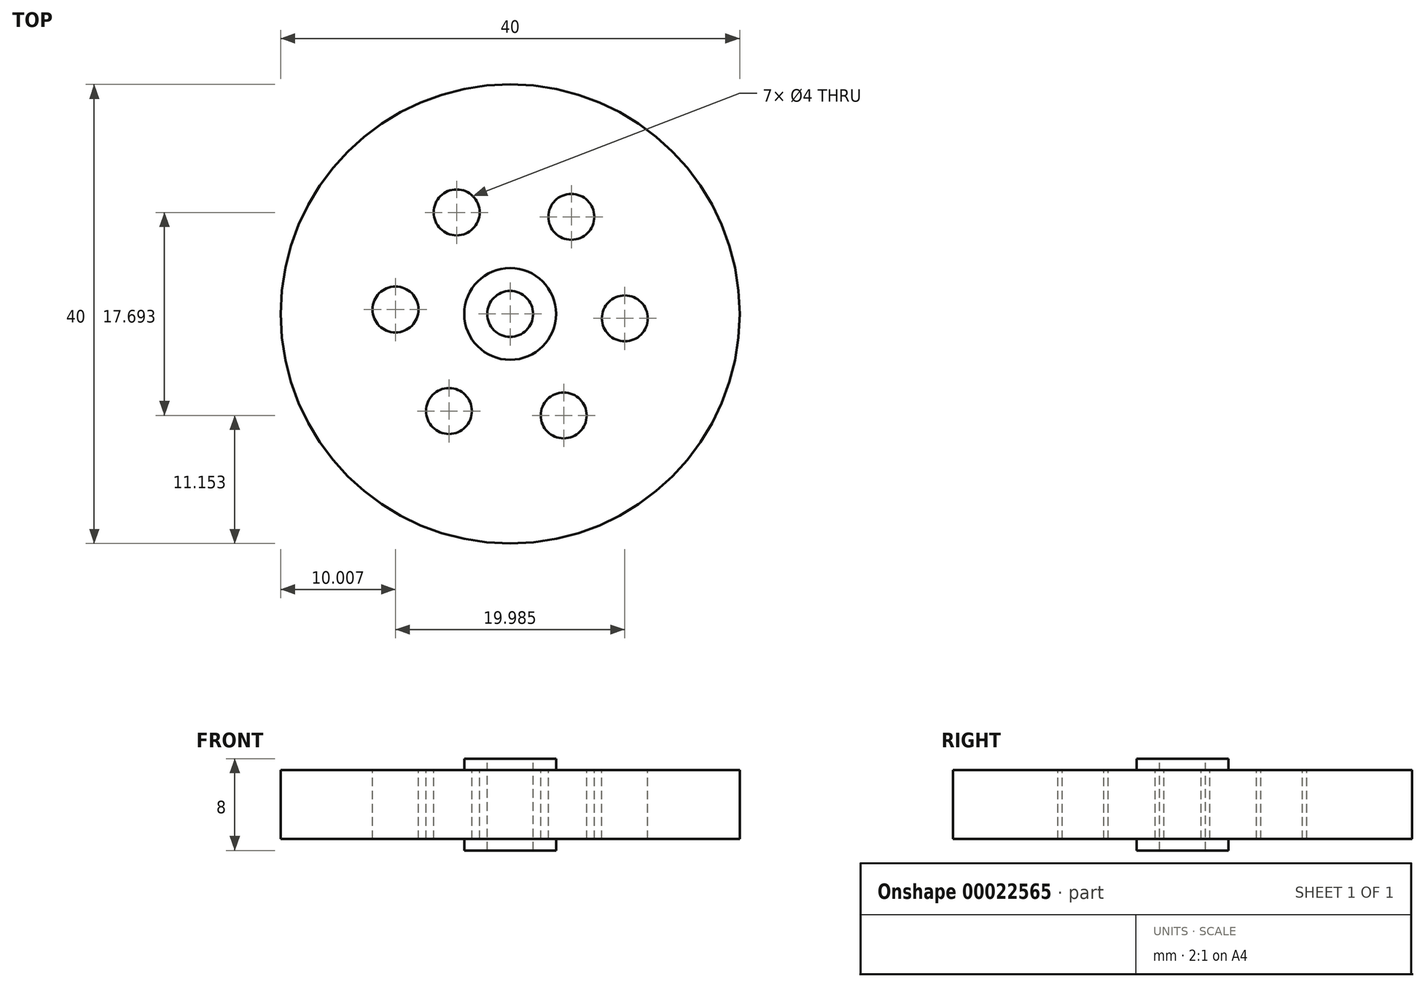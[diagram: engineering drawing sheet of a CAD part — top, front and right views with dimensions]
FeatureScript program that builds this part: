
annotation { "Feature Type Name" : "Feature", "Feature Type Description" : "" }
export const myFeature = defineFeature(function(context is Context, id is Id, definition is map)
    precondition{}
    {
        {
            var Q0;
            Q0=qCreatedBy(makeId("Top.planeOp"),FACE);
            var sketch = newSketch(context, id + "F0", { "sketchPlane" : qUnion([Q0])});
            skCircle(sketch, "E0", {"center": v(0, 0) * mm, "radius": 20 * mm});
            skSolve(sketch);
        }
        {
            var Q0;
            Q0=makeQuery(id+"F0.imprint","IMPRINT",FACE,{"disambiguationData":[TD([[makeQuery(id+"F0.imprint","IMPRINT",EDGE,{"derivedFrom":sQuery(id+"F0.wireOp",EDGE,"E0")}),1.0]])]});
            extrude(context, id + "F1", {"entities" : qUnion([Q0]), "depth" : 6 * mm});
        }
        {
            var Q0;
            Q0=makeQuery(id+"F1.opExtrude","CAP_FACE",FACE,{"disambiguationData":[OSD([sQuery(id+"F0.wireOp",EDGE,"E0")])],"isStart":false});
            var sketch = newSketch(context, id + "F2", { "sketchPlane" : qUnion([Q0])});
            skCircle(sketch, "E1", {"center": v(0, 0) * mm, "radius": 4 * mm});
            skCircle(sketch, "E2", {"center": v(0, 0) * mm, "radius": 2 * mm});
            skCircle(sketch, "E3", {"center": v(5.33, 8.46) * mm, "radius": 2 * mm});
            skCircle(sketch, "E4.1.0", {"center": v(-4.66, 8.85) * mm, "radius": 2 * mm});
            skCircle(sketch, "E4.2.0", {"center": v(-10, 0.39) * mm, "radius": 2 * mm});
            skCircle(sketch, "E4.3.0", {"center": v(-5.33, -8.46) * mm, "radius": 2 * mm});
            skCircle(sketch, "E4.4.0", {"center": v(4.66, -8.85) * mm, "radius": 2 * mm});
            skCircle(sketch, "E4.5.0", {"center": v(10, -0.39) * mm, "radius": 2 * mm});
            skSolve(sketch);
        }
        {
            var Q0;
            Q0=makeQuery(id+"F2.imprint","IMPRINT",FACE,{"disambiguationData":[TD([[makeQuery(id+"F2.imprint","IMPRINT",EDGE,{"derivedFrom":sQuery(id+"F2.wireOp",EDGE,"E4.1.0")}),1.0]])]});
            var Q1;
            Q1=makeQuery(id+"F2.imprint","IMPRINT",FACE,{"disambiguationData":[TD([[makeQuery(id+"F2.imprint","IMPRINT",EDGE,{"derivedFrom":sQuery(id+"F2.wireOp",EDGE,"E3")}),1.0]])]});
            var Q2;
            Q2=makeQuery(id+"F2.imprint","IMPRINT",FACE,{"disambiguationData":[TD([[makeQuery(id+"F2.imprint","IMPRINT",EDGE,{"derivedFrom":sQuery(id+"F2.wireOp",EDGE,"E4.5.0")}),1.0]])]});
            var Q3;
            Q3=makeQuery(id+"F2.imprint","IMPRINT",FACE,{"disambiguationData":[TD([[makeQuery(id+"F2.imprint","IMPRINT",EDGE,{"derivedFrom":sQuery(id+"F2.wireOp",EDGE,"E4.4.0")}),1.0]])]});
            var Q4;
            Q4=makeQuery(id+"F2.imprint","IMPRINT",FACE,{"disambiguationData":[TD([[makeQuery(id+"F2.imprint","IMPRINT",EDGE,{"derivedFrom":sQuery(id+"F2.wireOp",EDGE,"E4.3.0")}),1.0]])]});
            var Q5;
            Q5=makeQuery(id+"F2.imprint","IMPRINT",FACE,{"disambiguationData":[TD([[makeQuery(id+"F2.imprint","IMPRINT",EDGE,{"derivedFrom":sQuery(id+"F2.wireOp",EDGE,"E4.2.0")}),1.0]])]});
            var Q6;
            Q6=makeQuery(id+"F2.imprint","IMPRINT",FACE,{"disambiguationData":[TD([[makeQuery(id+"F2.imprint","IMPRINT",EDGE,{"derivedFrom":sQuery(id+"F2.wireOp",EDGE,"E2")}),1.0]])]});
            extrude(context, id + "F3", {"entities" : qUnion([Q0, Q1, Q2, Q3, Q4, Q5, Q6]), "operationType" : NewBodyOperationType.REMOVE, "endBound" : BoundingType.THROUGH_ALL, "oppositeDirection" : true, "depth" : 25.4 * mm});
        }
        {
            var Q0;
            Q0=makeQuery(id+"F2.imprint","IMPRINT",FACE,{"disambiguationData":[TD([[makeQuery(id+"F2.imprint","IMPRINT",EDGE,{"derivedFrom":sQuery(id+"F2.wireOp",EDGE,"E1")}),1.0]])]});
            extrude(context, id + "F4", {"entities" : qUnion([Q0]), "operationType" : NewBodyOperationType.ADD, "depth" : 1 * mm});
        }
        {
            var Q0;
            Q0=makeQuery(id+"F1.opExtrude","CAP_FACE",FACE,{"disambiguationData":[OSD([sQuery(id+"F0.wireOp",EDGE,"E0")])],"isStart":true});
            var sketch = newSketch(context, id + "F5", { "sketchPlane" : qUnion([Q0])});
            skCircle(sketch, "E5", {"center": v(0, 0) * mm, "radius": 4 * mm});
            skSolve(sketch);
        }
        {
            var Q0;
            Q0=makeQuery(id+"F5.imprint","IMPRINT",FACE,{"disambiguationData":[TD([[makeQuery(id+"F5.imprint","IMPRINT",EDGE,{"derivedFrom":sQuery(id+"F5.wireOp",EDGE,"E5")}),1.0]])]});
            extrude(context, id + "F6", {"entities" : qUnion([Q0]), "operationType" : NewBodyOperationType.ADD, "depth" : 1 * mm});
        }
    });
